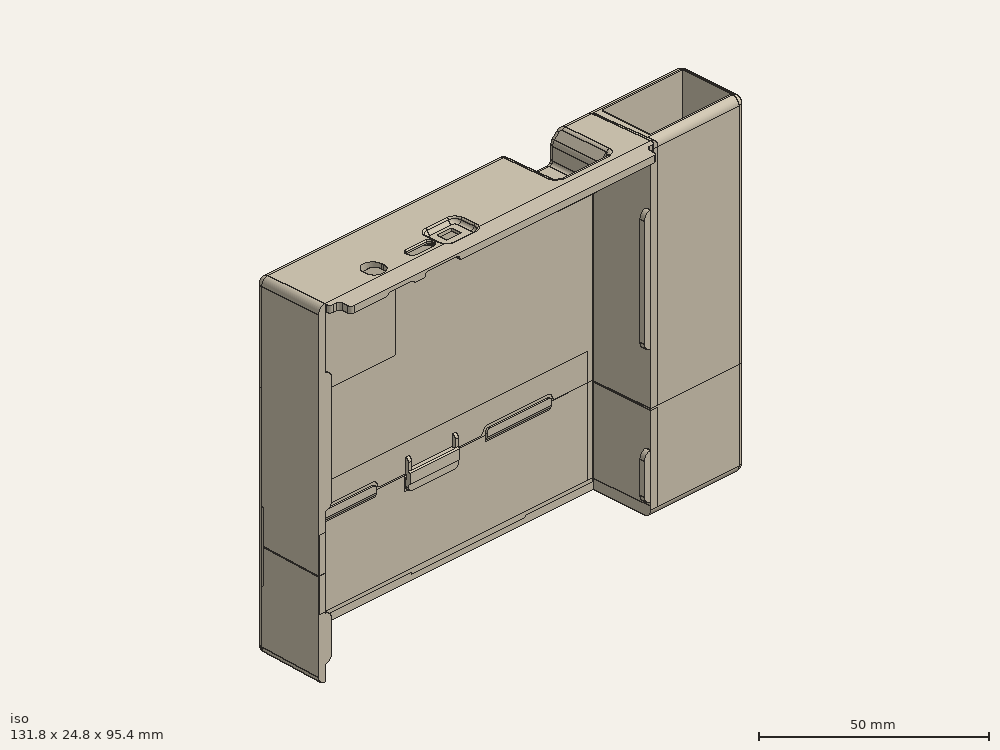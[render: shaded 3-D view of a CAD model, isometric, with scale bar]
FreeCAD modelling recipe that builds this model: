
FCSTD DOCUMENT  (FreeCAD 0.20R29177 +233 (Git))
Label: N2CaseOnePeice_10_12_2022
License: All rights reserved
LicenseURL: http://en.wikipedia.org/wiki/All_rights_reserved
objects: Part::Box×24, Part::Cylinder×12, Part::MultiFuse×11, Part::Cut×10, Part::Sphere×4, Part::Feature×2, Sketcher::SketchObject×2, PartDesign::Pad×2, PartDesign::Body×2
note: 71 computed .brp shape members not serialized (recipe doc carries the construction recipe); baked Part::Feature solids carry a one-line shape summary decoded from their .brp

FEATURE [Part::Feature] Solid  label="N2_BOTTOM_COVER"
  shape: bbox 104.6 x 25.21 x 71.78 mm, 343 faces (baked)
FEATURE [Part::Feature] Solid001  label="N2_TOP_COVER"
  shape: bbox 104.6 x 24.81 x 29.22 mm, 349 faces (baked)
FEATURE [Part::Box] Box  label="Cube"
  AttacherType = Attacher::AttachEngine3D
  Height = 15
  Length = 62.5
  Placement = pos=(-49,18,44) rot=(0,1,0;1.5708rad)
  Width = 2
FEATURE [Part::MultiFuse] Fusion  label="BottomCover"
  Shapes = -> [Solid,Box]
FEATURE [Part::Box] Box001  label="Cube001"
  AttacherType = Attacher::AttachEngine3D
  Height = 15
  Length = 97.5
  Placement = pos=(48.5,20,-3.5) rot=(0,1,0;3.14159rad)
  Width = 2
FEATURE [Part::Cut] Cut
  Base = -> Fusion
  Tool = -> Box001
FEATURE [Part::Box] Box002  label="usbEthernet"
  AttacherType = Attacher::AttachEngine3D
  Height = 25
  Length = 72
  Placement = pos=(52.5,2.6,47.4) rot=(0,1,0;1.5708rad)
  Width = 15
FEATURE [Part::Box] Box003  label="usbEthernetCover"
  AttacherType = Attacher::AttachEngine3D
  Height = 27.5
  Length = 72
  Placement = pos=(50.5,2.2,47.4) rot=(0,1,0;1.5708rad)
  Width = 15.85
FEATURE [Part::Box] Box004  label="usbEthernetCover001"
  AttacherType = Attacher::AttachEngine3D
  Height = 27.52
  Length = 65.19
  Placement = pos=(49.98,17.6,45.39) rot=(0,1,0;1.5708rad)
  Width = 2.4
FEATURE [Part::Box] Box005  label="usbEthernetCover002"
  AttacherType = Attacher::AttachEngine3D
  Height = 2
  Length = 65.19
  Placement = pos=(77.5,2.2,45.39) rot=(0,1,0;1.5708rad)
  Width = 15.8
FEATURE [Part::Cylinder] Cylinder
  Angle = 90
  AttacherType = Attacher::AttachEngine3D
  FirstAngle = 0
  Height = 65.2
  Placement = pos=(77.5,2.2,-19.8) rot=(0,0,-1;1.5708rad)
  Radius = 2
  SecondAngle = 0
FEATURE [Part::Cylinder] Cylinder001
  Angle = 90
  AttacherType = Attacher::AttachEngine3D
  FirstAngle = 0
  Height = 27.5
  Placement = pos=(77.5,18,45.4) rot=(0,-1,0;1.5708rad)
  Radius = 2
  SecondAngle = 0
FEATURE [Part::Cylinder] Cylinder002
  Angle = 90
  AttacherType = Attacher::AttachEngine3D
  FirstAngle = 0
  Height = 15.8
  Placement = pos=(77.5,2.2,45.4) rot=(0.57735,0.57735,0.57735;4.18879rad)
  Radius = 2
  SecondAngle = 0
FEATURE [Part::Cylinder] Cylinder003
  Angle = 90
  AttacherType = Attacher::AttachEngine3D
  FirstAngle = 0
  Height = 65.2
  Placement = pos=(77.5,18,-19.8) rot=(0,0,1;0rad)
  Radius = 2
  SecondAngle = 0
FEATURE [Part::Box] Box006  label="usbEthernetCover003"
  AttacherType = Attacher::AttachEngine3D
  Height = 27.2
  Length = 65.19
  Placement = pos=(50.3,0.2,45.39) rot=(0,1,0;1.5708rad)
  Width = 2.4
FEATURE [Part::Cylinder] Cylinder004
  Angle = 90
  AttacherType = Attacher::AttachEngine3D
  FirstAngle = 0
  Height = 26.4
  Placement = pos=(77.5,2.2,45.4) rot=(0.57735,-0.57735,-0.57735;2.0944rad)
  Radius = 2
  SecondAngle = 0
FEATURE [Part::Sphere] Sphere
  Angle1 = -90
  Angle2 = 90
  Angle3 = 360
  AttacherType = Attacher::AttachEngine3D
  Placement = pos=(77.5,18,45.4) rot=(0,0,1;0rad)
  Radius = 2
FEATURE [Part::Sphere] Sphere001
  Angle1 = -90
  Angle2 = 90
  Angle3 = 360
  AttacherType = Attacher::AttachEngine3D
  Placement = pos=(77.5,2.2,45.4) rot=(0,0,1;0rad)
  Radius = 2
FEATURE [Part::MultiFuse] Fusion001  label="usbCover"
  Shapes = -> [Box003,Box004,Box005,Cylinder,Cylinder001,Cylinder002,Cylinder003,Box006,Cylinder004,Sphere,Sphere001]
FEATURE [Part::MultiFuse] Fusion002
  Shapes = -> [Cut,Fusion001]
FEATURE [Part::Cut] Cut001  label="front"
  Base = -> Fusion002
  Tool = -> Box002
FEATURE [Part::Box] Box007  label="Cube002"
  AttacherType = Attacher::AttachEngine3D
  Height = 10
  Length = 30
  Placement = pos=(79.5,0,-19.8) rot=(0,1,0;3.14159rad)
  Width = 20
FEATURE [Part::Cut] Cut002
  Base = -> Cut001
  Tool = -> Box007
FEATURE [Part::Box] Box008  label="Cube003"
  AttacherType = Attacher::AttachEngine3D
  Height = 10
  Length = 30
  Placement = pos=(79.5,0,-19.8) rot=(0,1,0;3.14159rad)
  Width = 20
FEATURE [Part::Cut] Cut003  label="front001"
  Base = -> Cut002
  Tool = -> Box008
FEATURE [Part::Box] Box009  label="usbEthernet001"
  AttacherType = Attacher::AttachEngine3D
  Height = 25
  Length = 72
  Placement = pos=(52.5,2.6,6.3) rot=(0,1,0;1.5708rad)
  Width = 15
FEATURE [Part::Box] Box010  label="usbEthernetCover004"
  AttacherType = Attacher::AttachEngine3D
  Height = 27.5
  Length = 72
  Placement = pos=(50.5,2.2,-19.8) rot=(0,1,0;1.5708rad)
  Width = 15.85
FEATURE [Part::Box] Box011  label="usbEthernetCover005"
  AttacherType = Attacher::AttachEngine3D
  Height = 27.52
  Length = 65.19
  Placement = pos=(49.98,17.6,-19.8) rot=(0,1,0;1.5708rad)
  Width = 2.4
FEATURE [Part::Box] Box012  label="usbEthernetCover006"
  AttacherType = Attacher::AttachEngine3D
  Height = 2
  Length = 65.19
  Placement = pos=(77.5,2.2,-19.8) rot=(0,1,0;1.5708rad)
  Width = 15.8
FEATURE [Part::Box] Box013  label="usbEthernetCover007"
  AttacherType = Attacher::AttachEngine3D
  Height = 27.2
  Length = 65.19
  Placement = pos=(50.3,0.2,-19.8) rot=(0,1,0;1.5708rad)
  Width = 2.4
FEATURE [Part::Box] Box016  label="Cube005"
  AttacherType = Attacher::AttachEngine3D
  Height = 50
  Length = 29.5
  Placement = pos=(79.5,0,-45.4) rot=(0,1,0;3.14159rad)
  Width = 20
FEATURE [Part::MultiFuse] Fusion003
  Shapes = -> [Solid001,Box010,Box011,Box012,Box013]
FEATURE [Part::Cut] Cut004
  Base = -> Fusion003
  Tool = -> Box016
FEATURE [Part::Cut] Cut005
  Base = -> Cut004
  Tool = -> Box009
FEATURE [Part::Box] Box017  label="Cube006"
  AttacherType = Attacher::AttachEngine3D
  Height = 50
  Length = 23.5
  Placement = pos=(73.4,17.6,-45.39) rot=(0,1,0;3.14159rad)
  Width = 20
FEATURE [Part::Cut] Cut006
  Base = -> Cut005
  Tool = -> Box017
FEATURE [Part::Cylinder] Cylinder005
  Angle = 90
  AttacherType = Attacher::AttachEngine3D
  FirstAngle = 0
  Height = 65.2
  Placement = pos=(77.5,2.2,-45.4) rot=(0,0,-1;1.5708rad)
  Radius = 2
  SecondAngle = 0
FEATURE [Part::Cylinder] Cylinder006
  Angle = 90
  AttacherType = Attacher::AttachEngine3D
  FirstAngle = 0
  Height = 27.5
  Placement = pos=(77.5,18,-45.4) rot=(0,-1,0;1.5708rad)
  Radius = 2
  SecondAngle = 0
FEATURE [Part::Cylinder] Cylinder007
  Angle = 90
  AttacherType = Attacher::AttachEngine3D
  FirstAngle = 0
  Height = 15.8
  Placement = pos=(77.5,2.2,-45.4) rot=(-1,0,0;1.5708rad)
  Radius = 2
  SecondAngle = 0
FEATURE [Part::Cylinder] Cylinder008
  Angle = 90
  AttacherType = Attacher::AttachEngine3D
  FirstAngle = 0
  Height = 65.2
  Placement = pos=(77.5,18,-45.4) rot=(0,0,1;0rad)
  Radius = 2
  SecondAngle = 0
FEATURE [Part::Cylinder] Cylinder009
  Angle = 90
  AttacherType = Attacher::AttachEngine3D
  FirstAngle = 0
  Height = 27.6
  Placement = pos=(77.5,2.2,-45.4) rot=(0.707107,0,-0.707107;3.14159rad)
  Radius = 2
  SecondAngle = 0
FEATURE [Part::Cylinder] Cylinder010
  Angle = 90
  AttacherType = Attacher::AttachEngine3D
  FirstAngle = 0
  Height = 27.6
  Placement = pos=(77.5,18,-45.4) rot=(0.57735,0.57735,-0.57735;4.18879rad)
  Radius = 2
  SecondAngle = 0
FEATURE [Part::Box] Box018  label="Cube007"
  AttacherType = Attacher::AttachEngine3D
  Height = 2
  Length = 27.6
  Placement = pos=(49.9,18,-45.4) rot=(1,0,0;3.14159rad)
  Width = 15.8
FEATURE [Part::Box] Box019  label="usbEthernet002"
  AttacherType = Attacher::AttachEngine3D
  Height = 25
  Length = 72
  Placement = pos=(52.5,2.6,-2.5) rot=(0,1,0;1.5708rad)
  Width = 15
FEATURE [Part::Sphere] Sphere002
  Angle1 = -90
  Angle2 = 90
  Angle3 = 360
  AttacherType = Attacher::AttachEngine3D
  Placement = pos=(77.5,18,-45.4) rot=(0,0,1;0rad)
  Radius = 2
FEATURE [Part::Sphere] Sphere003
  Angle1 = -90
  Angle2 = 90
  Angle3 = 360
  AttacherType = Attacher::AttachEngine3D
  Placement = pos=(77.5,2.2,-45.4) rot=(0,0,1;0rad)
  Radius = 2
FEATURE [Part::Box] Box020  label="Cube008"
  AttacherType = Attacher::AttachEngine3D
  Height = 40
  Length = 10
  Placement = pos=(73.6,0,-19.8) rot=(0,0,1;0rad)
  Width = 22
FEATURE [Part::MultiFuse] Fusion004  label="cuts"
  Shapes = -> [Box020,Box019]
FEATURE [Part::MultiFuse] Fusion005
  Shapes = -> [Sphere003,Cut006,Cylinder005,Cylinder006,Cylinder007,Cylinder008,Cylinder009,Cylinder010,Box018,Sphere002]
FEATURE [Part::Cut] Cut007  label="back"
  Base = -> Fusion005
  Tool = -> Fusion004
FEATURE [Part::Box] Box021  label="Cube009"
  AttacherType = Attacher::AttachEngine3D
  Height = 32.5
  Length = 97.5
  Placement = pos=(48.5,18,-11.9) rot=(0,1,0;3.14159rad)
  Width = 2
FEATURE [Part::Box] Box068  label="logoBase001"
  AttacherType = Attacher::AttachEngine3D
  Height = 30
  Length = 35
  Placement = pos=(21.5,-44,15.25) rot=(0,0,1;0rad)
  Width = 1.8
FEATURE [Sketcher::SketchObject] Sketch001
  FullyConstrained = false
  MapMode = 5
  Support = -> [XY_Plane001]
  sketch-geometry (205):
    g0: LineSegment StartX=-15.0667 StartY=-2.9879 StartZ=0 EndX=-14.4175 EndY=-3.20194 EndZ=0
    g1: LineSegment StartX=-14.1386 StartY=-3.3581 StartZ=0 EndX=-13.8673 EndY=-3.55064 EndZ=0
    g2: LineSegment StartX=-10.8098 StartY=-4.00788 StartZ=0 EndX=-10.5716 EndY=-4.29909 EndZ=0
    g3: LineSegment StartX=-10.5716 StartY=-4.29909 StartZ=0 EndX=-10.1338 EndY=-4.33136 EndZ=0
    g4: LineSegment StartX=-10.1338 StartY=-4.33136 StartZ=0 EndX=-9.89036 EndY=-4.3898 EndZ=0
    g5: LineSegment StartX=-9.51656 StartY=-5.73022 StartZ=0 EndX=-9.24931 EndY=-5.76229 EndZ=0
    g6: LineSegment StartX=-9.24931 StartY=-5.76229 StartZ=0 EndX=-8.92861 EndY=-5.90126 EndZ=0
    g7: LineSegment StartX=-8.92861 StartY=-5.90126 StartZ=0 EndX=-8.54378 EndY=-5.86384 EndZ=0
    g8: LineSegment StartX=-8.54378 StartY=-5.86384 StartZ=0 EndX=-7.71788 EndY=-5.75845 EndZ=0
    g9: LineSegment StartX=-7.71788 StartY=-5.75845 StartZ=0 EndX=-7.37291 EndY=-5.97257 EndZ=0
    g10: LineSegment StartX=-7.37291 StartY=-5.97257 StartZ=0 EndX=-6.72487 EndY=-5.72038 EndZ=0
    g11: LineSegment StartX=-6.72487 StartY=-5.72038 StartZ=0 EndX=-6.27066 EndY=-5.69481 EndZ=0
    g12: LineSegment StartX=-6.27066 StartY=-5.69481 StartZ=0 EndX=-6.06223 EndY=-5.80493 EndZ=0
    g13: LineSegment StartX=-6.06223 StartY=-5.80493 StartZ=0 EndX=-5.35089 EndY=-5.48914 EndZ=0
    g14: LineSegment StartX=-5.35089 StartY=-5.48914 StartZ=0 EndX=-5.02402 EndY=-5.48914 EndZ=0
    g15: LineSegment StartX=-5.02402 StartY=-5.48914 StartZ=0 EndX=-4.80126 EndY=-5.53132 EndZ=0
    g16: LineSegment StartX=-4.80126 StartY=-5.53132 StartZ=0 EndX=-4.19735 EndY=-5.16248 EndZ=0
    g17: LineSegment StartX=-3.75191 StartY=-4.97251 StartZ=0 EndX=-3.37714 EndY=-4.97251 EndZ=0
    g18: LineSegment StartX=-3.37714 StartY=-4.97251 StartZ=0 EndX=-2.81898 EndY=-4.45422 EndZ=0
    g19: LineSegment StartX=-2.81898 StartY=-4.45422 StartZ=0 EndX=-2.62761 EndY=-4.34259 EndZ=0
    g20: LineSegment StartX=-2.62761 StartY=-4.34259 StartZ=0 EndX=-2.15112 EndY=-4.35765 EndZ=0
    g21: LineSegment StartX=-2.38042 StartY=-4.51801 StartZ=0 EndX=-3.18577 EndY=-5.42702 EndZ=0
    g22: LineSegment StartX=-3.18577 StartY=-5.42702 StartZ=0 EndX=-3.61318 EndY=-6.05824 EndZ=0
    g23: LineSegment StartX=-3.61318 StartY=-6.05824 StartZ=0 EndX=-3.7111 EndY=-6.64579 EndZ=0
    g24: LineSegment StartX=-3.7111 StartY=-6.64579 StartZ=0 EndX=-3.83514 EndY=-7.15501 EndZ=0
    g25: LineSegment StartX=-3.83514 StartY=-7.15501 StartZ=0 EndX=-3.75878 EndY=-7.50876 EndZ=0
    g26: LineSegment StartX=-3.75878 StartY=-7.50876 StartZ=0 EndX=-3.70596 EndY=-7.68135 EndZ=0
    g27: LineSegment StartX=-3.70596 StartY=-7.68135 StartZ=0 EndX=-3.53967 EndY=-7.85202 EndZ=0
    g28: LineSegment StartX=-3.53967 StartY=-7.85202 StartZ=0 EndX=-3.4685 EndY=-8.65617 EndZ=0
    g29: LineSegment StartX=-3.27268 StartY=-8.56671 StartZ=0 EndX=-3.16823 EndY=-8.76909 EndZ=0
    g30: LineSegment StartX=-3.07088 StartY=-9.32083 StartZ=0 EndX=-2.84207 EndY=-9.3355 EndZ=0
    g31: LineSegment StartX=-2.84207 StartY=-9.3355 StartZ=0 EndX=-2.45193 EndY=-10.0982 EndZ=0
    g32: LineSegment StartX=-2.45193 StartY=-10.0982 StartZ=0 EndX=-2.24953 EndY=-10.1304 EndZ=0
    g33: LineSegment StartX=-2.24953 StartY=-10.1304 StartZ=0 EndX=-0.96042 EndY=-11.8753 EndZ=0
    g34: LineSegment StartX=-0.96042 StartY=-11.8753 StartZ=0 EndX=-0.153326 EndY=-11.3889 EndZ=0
    g35: LineSegment StartX=-0.153326 StartY=-11.3889 StartZ=0 EndX=0.461347 EndY=-10.7689 EndZ=0
    g36: LineSegment StartX=0.461347 StartY=-10.7689 StartZ=0 EndX=0.669802 EndY=-10.7261 EndZ=0
    g37: LineSegment StartX=0.669802 StartY=-10.7261 StartZ=0 EndX=1.31724 EndY=-9.70998 EndZ=0
    g38: LineSegment StartX=1.31724 StartY=-9.70998 StartZ=0 EndX=1.51826 EndY=-9.65081 EndZ=0
    g39: LineSegment StartX=1.51826 StartY=-9.65081 StartZ=0 EndX=1.74022 EndY=-9.08937 EndZ=0
    g40: LineSegment StartX=1.74022 StartY=-9.08937 StartZ=0 EndX=2.02094 EndY=-9.04367 EndZ=0
    g41: LineSegment StartX=2.02094 StartY=-9.04367 StartZ=0 EndX=2.39306 EndY=-7.80327 EndZ=0
    g42: LineSegment StartX=2.39306 StartY=-7.80327 StartZ=0 EndX=2.58839 EndY=-7.69871 EndZ=0
    g43: LineSegment StartX=2.6542 StartY=-7.03945 StartZ=0 EndX=2.86963 EndY=-6.81749 EndZ=0
    g44: LineSegment StartX=2.86963 StartY=-6.81749 StartZ=0 EndX=3.0916 EndY=-6.92847 EndZ=0
    g45: LineSegment StartX=3.0916 StartY=-6.92847 StartZ=0 EndX=3.79666 EndY=-7.57478 EndZ=0
    g46: LineSegment StartX=3.79666 StartY=-7.57478 StartZ=0 EndX=3.93376 EndY=-7.50297 EndZ=0
    g47: LineSegment StartX=3.93376 StartY=-7.50297 StartZ=0 EndX=4.46256 EndY=-7.97301 EndZ=0
    g48: LineSegment StartX=4.46256 StartY=-7.97301 StartZ=0 EndX=4.68452 EndY=-7.92079 EndZ=0
    g49: LineSegment StartX=4.68452 StartY=-7.92079 StartZ=0 EndX=5.1154 EndY=-8.34513 EndZ=0
    g50: LineSegment StartX=5.1154 StartY=-8.34513 StartZ=0 EndX=5.32431 EndY=-8.28637 EndZ=0
    g51: LineSegment StartX=5.32431 StartY=-8.28637 StartZ=0 EndX=6.23668 EndY=-8.79564 EndZ=0
    g52: LineSegment StartX=6.23668 StartY=-8.79564 StartZ=0 EndX=6.50362 EndY=-8.76631 EndZ=0
    g53: LineSegment StartX=6.50362 StartY=-8.76631 StartZ=0 EndX=7.14802 EndY=-9.05537 EndZ=0
    g54: LineSegment StartX=7.14802 StartY=-9.05537 StartZ=0 EndX=8.04883 EndY=-9.18613 EndZ=0
    g55: LineSegment StartX=8.04883 StartY=-9.18613 StartZ=0 EndX=8.36847 EndY=-7.93662 EndZ=0
    g56: LineSegment StartX=8.36847 StartY=-7.93662 StartZ=0 EndX=8.49923 EndY=-7.79133 EndZ=0
    g57: LineSegment StartX=8.49923 StartY=-7.79133 StartZ=0 EndX=8.43477 EndY=-6.72206 EndZ=0
    g58: LineSegment StartX=8.43477 StartY=-6.72206 StartZ=0 EndX=8.58621 EndY=-6.47988 EndZ=0
    g59: LineSegment StartX=8.58621 StartY=-6.47988 StartZ=0 EndX=8.32296 EndY=-5.53178 EndZ=0
    g60: LineSegment StartX=8.32296 StartY=-5.53178 StartZ=0 EndX=8.43984 EndY=-5.19091 EndZ=0
    g61: LineSegment StartX=8.43984 StartY=-5.19091 StartZ=0 EndX=8.07426 EndY=-4.39307 EndZ=0
    g62: LineSegment StartX=8.07426 StartY=-4.39307 StartZ=0 EndX=8.04236 EndY=-4.17777 EndZ=0
    g63: LineSegment StartX=8.04236 StartY=-4.17777 StartZ=0 EndX=8.0902 EndY=-3.99438 EndZ=0
    g64: LineSegment StartX=8.4103 StartY=-4.11103 StartZ=0 EndX=8.72013 EndY=-4.0502 EndZ=0
    g65: LineSegment StartX=8.72013 StartY=-4.0502 StartZ=0 EndX=9.31817 EndY=-4.0502 EndZ=0
    g66: LineSegment StartX=9.31817 StartY=-4.0502 StartZ=0 EndX=9.82964 EndY=-4.15887 EndZ=0
    g67: LineSegment StartX=10.1326 StartY=-3.9675 StartZ=0 EndX=10.5175 EndY=-3.9623 EndZ=0
    g68: LineSegment StartX=10.5175 StartY=-3.9623 StartZ=0 EndX=10.8831 EndY=-3.97536 EndZ=0
    g69: LineSegment StartX=10.8831 StartY=-3.97536 StartZ=0 EndX=11.2245 EndY=-4.09431 EndZ=0
    g70: LineSegment StartX=11.2245 StartY=-4.09431 StartZ=0 EndX=11.6861 EndY=-3.91007 EndZ=0
    g71: LineSegment StartX=11.6861 StartY=-3.91007 StartZ=0 EndX=12.1039 EndY=-3.88396 EndZ=0
    g72: LineSegment StartX=12.1039 StartY=-3.88396 StartZ=0 EndX=12.6 EndY=-3.9623 EndZ=0
    g73: LineSegment StartX=12.6 StartY=-3.9623 StartZ=0 EndX=13.5793 EndY=-3.87743 EndZ=0
    g74: LineSegment StartX=13.5793 StartY=-3.87743 StartZ=0 EndX=14.3888 EndY=-3.74687 EndZ=0
    g75: LineSegment StartX=14.3888 StartY=-3.74687 StartZ=0 EndX=14.7544 EndY=-3.68158 EndZ=0
    g76: LineSegment StartX=14.7544 StartY=-3.68158 StartZ=0 EndX=15.2767 EndY=-3.75339 EndZ=0
    g77: LineSegment StartX=15.2767 StartY=-3.75339 StartZ=0 EndX=15.0432 EndY=-3.24137 EndZ=0
    g78: LineSegment StartX=15.0432 StartY=-3.24137 StartZ=0 EndX=14.5209 EndY=-2.51672 EndZ=0
    g79: LineSegment StartX=14.5209 StartY=-2.51672 StartZ=0 EndX=14.0378 EndY=-1.99445 EndZ=0
    g80: LineSegment StartX=14.0378 StartY=-1.99445 StartZ=0 EndX=13.2802 EndY=-1.54625 EndZ=0
    g81: LineSegment StartX=13.2802 StartY=-1.54625 StartZ=0 EndX=13.0438 EndY=-1.23117 EndZ=0
    g82: LineSegment StartX=13.0438 StartY=-1.23117 StartZ=0 EndX=12.1074 EndY=-0.797939 EndZ=0
    g83: LineSegment StartX=12.1074 StartY=-0.797939 StartZ=0 EndX=11.3804 EndY=-0.250878 EndZ=0
    g84: LineSegment StartX=11.3804 StartY=-0.250878 StartZ=0 EndX=10.4396 EndY=0.304889 EndZ=0
    g85: LineSegment StartX=10.4396 StartY=0.304889 StartZ=0 EndX=9.59526 EndY=0.727998 EndZ=0
    g86: LineSegment StartX=9.59526 StartY=0.727998 StartZ=0 EndX=8.53624 EndY=0.97306 EndZ=0
    g87: LineSegment StartX=8.53624 StartY=0.97306 StartZ=0 EndX=7.199 EndY=0.97306 EndZ=0
    g88: LineSegment StartX=7.199 StartY=0.97306 StartZ=0 EndX=5.77932 EndY=0.795578 EndZ=0
    g89: LineSegment StartX=5.77932 StartY=0.795578 StartZ=0 EndX=5.60186 EndY=0.795578 EndZ=0
    g90: LineSegment StartX=5.60186 StartY=0.795578 StartZ=0 EndX=5.83178 EndY=0.981815 EndZ=0
    g91: LineSegment StartX=5.83178 StartY=0.981815 StartZ=0 EndX=6.25403 EndY=1.1582 EndZ=0
    g92: LineSegment StartX=6.30214 StartY=1.38269 StartZ=0 EndX=7.17987 EndY=1.70686 EndZ=0
    g93: LineSegment StartX=7.17987 StartY=1.70686 StartZ=0 EndX=7.44682 EndY=1.79438 EndZ=0
    g94: LineSegment StartX=7.44682 StartY=1.79438 StartZ=0 EndX=7.49058 EndY=2.12696 EndZ=0
    g95: LineSegment StartX=7.49058 StartY=2.12696 StartZ=0 EndX=8.30058 EndY=2.66839 EndZ=0
    g96: LineSegment StartX=8.30058 StartY=2.66839 StartZ=0 EndX=8.68575 EndY=2.81854 EndZ=0
    g97: LineSegment StartX=8.68575 StartY=2.81854 StartZ=0 EndX=8.68575 EndY=3.12537 EndZ=0
    g98: LineSegment StartX=8.68575 StartY=3.12537 StartZ=0 EndX=8.89508 EndY=3.18684 EndZ=0
    g99: LineSegment StartX=8.89508 StartY=3.18684 StartZ=0 EndX=9.63492 EndY=4.06602 EndZ=0
    g100: LineSegment StartX=9.63492 StartY=4.06602 StartZ=0 EndX=9.62638 EndY=4.32743 EndZ=0
    g101: LineSegment StartX=9.62638 StartY=4.32743 StartZ=0 EndX=10.2068 EndY=5.18314 EndZ=0
    g102: LineSegment StartX=10.2068 StartY=5.18314 StartZ=0 EndX=9.25518 EndY=5.64445 EndZ=0
    g103: LineSegment StartX=9.1102 StartY=5.87597 StartZ=0 EndX=8.32132 EndY=5.97336 EndZ=0
    g104: LineSegment StartX=8.32132 StartY=5.97336 StartZ=0 EndX=8.15466 EndY=6.06625 EndZ=0
    g105: LineSegment StartX=7.63471 StartY=6.13088 StartZ=0 EndX=7.56391 EndY=6.33267 EndZ=0
    g106: LineSegment StartX=7.56391 StartY=6.33267 StartZ=0 EndX=6.74832 EndY=6.35496 EndZ=0
    g107: LineSegment StartX=6.74832 StartY=6.35496 StartZ=0 EndX=6.46819 EndY=6.29526 EndZ=0
    g108: LineSegment StartX=6.46819 StartY=6.29526 StartZ=0 EndX=6.27042 EndY=6.61061 EndZ=0
    g109: LineSegment StartX=6.27042 StartY=6.61061 StartZ=0 EndX=5.40453 EndY=6.33267 EndZ=0
    g110: LineSegment StartX=5.40453 StartY=6.33267 StartZ=0 EndX=5.27091 EndY=6.47164 EndZ=0
    g111: LineSegment StartX=5.27091 StartY=6.47164 StartZ=0 EndX=4.56942 EndY=6.24725 EndZ=0
    g112: LineSegment StartX=4.56942 StartY=6.24725 StartZ=0 EndX=4.44161 EndY=6.40652 EndZ=0
    g113: LineSegment StartX=4.44161 StartY=6.40652 StartZ=0 EndX=3.4195 EndY=5.94588 EndZ=0
    g114: LineSegment StartX=3.4195 StartY=5.94588 StartZ=0 EndX=3.29192 EndY=6.1532 EndZ=0
    g115: LineSegment StartX=3.29192 StartY=6.1532 StartZ=0 EndX=2.15964 EndY=5.49137 EndZ=0
    g116: LineSegment StartX=2.15964 StartY=5.49137 StartZ=0 EndX=2.00016 EndY=5.69869 EndZ=0
    g117: LineSegment StartX=2.00016 StartY=5.69869 StartZ=0 EndX=1.6185 EndY=5.34828 EndZ=0
    g118: LineSegment StartX=1.6185 StartY=5.34828 StartZ=0 EndX=1.45984 EndY=5.94974 EndZ=0
    g119: LineSegment StartX=1.38165 StartY=6.28651 StartZ=0 EndX=1.14534 EndY=6.29963 EndZ=0
    g120: LineSegment StartX=0.348522 StartY=7.29544 StartZ=0 EndX=0.126706 EndY=7.68126 EndZ=0
    g121: LineSegment StartX=0.126706 StartY=7.68126 StartZ=0 EndX=-0.415308 EndY=8.18163 EndZ=0
    g122: LineSegment StartX=-0.415308 StartY=8.18163 StartZ=0 EndX=-0.872658 EndY=8.6237 EndZ=0
    g123: LineSegment StartX=-0.872658 StartY=8.6237 StartZ=0 EndX=-1.12074 EndY=8.64329 EndZ=0
    g124: LineSegment StartX=-1.12074 StartY=8.64329 StartZ=0 EndX=-1.79316 EndY=9.11986 EndZ=0
    g125: LineSegment StartX=-1.79316 StartY=9.11986 StartZ=0 EndX=-2.31488 EndY=9.12122 EndZ=0
    g126: LineSegment StartX=-2.31488 StartY=9.12122 StartZ=0 EndX=-2.71321 EndY=9.13846 EndZ=0
    g127: LineSegment StartX=-2.71321 StartY=9.13846 StartZ=0 EndX=-2.88425 EndY=9.34157 EndZ=0
    g128: LineSegment StartX=-2.88425 StartY=9.34157 StartZ=0 EndX=-3.16779 EndY=9.26454 EndZ=0
    g129: LineSegment StartX=-3.70739 StartY=9.82796 StartZ=0 EndX=-4.04915 EndY=9.7003 EndZ=0
    g130: LineSegment StartX=-4.04915 StartY=9.7003 StartZ=0 EndX=-4.42988 EndY=10.011 EndZ=0
    g131: LineSegment StartX=-5.98947 StartY=10.3656 StartZ=0 EndX=-7.32605 EndY=10.4108 EndZ=0
    g132: LineSegment StartX=-7.25254 StartY=9.13254 StartZ=0 EndX=-7.36878 EndY=8.7693 EndZ=0
    g133: LineSegment StartX=-7.36878 StartY=8.7693 StartZ=0 EndX=-7.2614 EndY=7.83762 EndZ=0
    g134: LineSegment StartX=-7.2614 StartY=7.83762 StartZ=0 EndX=-7.41112 EndY=7.6042 EndZ=0
    g135: LineSegment StartX=-7.41112 StartY=7.6042 StartZ=0 EndX=-7.09216 EndY=6.74302 EndZ=0
    g136: LineSegment StartX=-7.09216 StartY=6.74302 StartZ=0 EndX=-7.10014 EndY=6.55962 EndZ=0
    g137: LineSegment StartX=-7.10014 StartY=6.55962 StartZ=0 EndX=-7.29151 EndY=6.3842 EndZ=0
    g138: LineSegment StartX=-7.29151 StartY=6.3842 StartZ=0 EndX=-6.74132 EndY=5.29976 EndZ=0
    g139: LineSegment StartX=-6.74132 StartY=5.29976 StartZ=0 EndX=-6.87495 EndY=5.02732 EndZ=0
    g140: LineSegment StartX=-6.87495 StartY=5.02732 StartZ=0 EndX=-6.31586 EndY=4.42065 EndZ=0
    g141: LineSegment StartX=-6.31586 StartY=4.42065 StartZ=0 EndX=-6.30396 EndY=4.19463 EndZ=0
    g142: LineSegment StartX=-6.30396 StartY=4.19463 StartZ=0 EndX=-6.05415 EndY=4.0043 EndZ=0
    g143: LineSegment StartX=-6.05415 StartY=4.0043 StartZ=0 EndX=-6.18501 EndY=3.95672 EndZ=0
    g144: LineSegment StartX=-6.18501 StartY=3.95672 StartZ=0 EndX=-5.54265 EndY=3.07645 EndZ=0
    g145: LineSegment StartX=-5.54265 StartY=3.07645 StartZ=0 EndX=-5.57833 EndY=2.90991 EndZ=0
    g146: LineSegment StartX=-5.57833 StartY=2.90991 StartZ=0 EndX=-5.1263 EndY=2.41029 EndZ=0
    g147: LineSegment StartX=-5.1263 StartY=2.41029 StartZ=0 EndX=-5.18578 EndY=2.26755 EndZ=0
    g148: LineSegment StartX=-5.18578 StartY=2.26755 StartZ=0 EndX=-4.73375 EndY=1.89878 EndZ=0
    g149: LineSegment StartX=-4.73375 StartY=1.89878 StartZ=0 EndX=-4.42446 EndY=1.5895 EndZ=0
    g150: LineSegment StartX=-4.42446 StartY=1.5895 StartZ=0 EndX=-5.31663 EndY=1.29211 EndZ=0
    g151: LineSegment StartX=-5.31663 StartY=1.29211 StartZ=0 EndX=-5.84004 EndY=1.08988 EndZ=0
    g152: LineSegment StartX=-5.84004 StartY=1.08988 StartZ=0 EndX=-6.04226 EndY=0.792495 EndZ=0
    g153: LineSegment StartX=-6.04226 StartY=0.792495 StartZ=0 EndX=-6.94632 EndY=0.994719 EndZ=0
    g154: LineSegment StartX=-6.94632 StartY=0.994719 StartZ=0 EndX=-7.19613 EndY=0.887659 EndZ=0
    g155: LineSegment StartX=-7.19613 StartY=0.887659 StartZ=0 EndX=-7.8147 EndY=1.0423 EndZ=0
    g156: LineSegment StartX=-7.8147 StartY=1.0423 StartZ=0 EndX=-8.02502 EndY=0.969153 EndZ=0
    g157: LineSegment StartX=-8.02502 StartY=0.969153 StartZ=0 EndX=-8.60267 EndY=1.03042 EndZ=0
    g158: LineSegment StartX=-8.60267 StartY=1.03042 StartZ=0 EndX=-8.8346 EndY=0.872878 EndZ=0
    g159: LineSegment StartX=-8.8346 StartY=0.872878 StartZ=0 EndX=-9.33349 EndY=0.929767 EndZ=0
    g160: LineSegment StartX=-9.33349 StartY=0.929767 StartZ=0 EndX=-9.66169 EndY=0.649695 EndZ=0
    g161: LineSegment StartX=-9.66169 StartY=0.649695 StartZ=0 EndX=-10.3249 EndY=0.649695 EndZ=0
    g162: LineSegment StartX=-10.3249 StartY=0.649695 StartZ=0 EndX=-11.0107 EndY=0.32425 EndZ=0
    g163: LineSegment StartX=-11.0107 StartY=0.32425 StartZ=0 EndX=-11.7283 EndY=0.053139 EndZ=0
    g164: LineSegment StartX=-11.7283 StartY=0.053139 StartZ=0 EndX=-12.2971 EndY=-0.13161 EndZ=0
    g165: LineSegment StartX=-12.2971 StartY=-0.13161 StartZ=0 EndX=-12.4212 EndY=-0.347049 EndZ=0
    g166: LineSegment StartX=-12.4212 StartY=-0.347049 StartZ=0 EndX=-13.296 EndY=-0.817096 EndZ=0
    g167: LineSegment StartX=-13.296 StartY=-0.817096 StartZ=0 EndX=-13.9227 EndY=-1.24144 EndZ=0
    g168: LineSegment StartX=-13.9227 StartY=-1.24144 StartZ=0 EndX=-14.1708 EndY=-1.59398 EndZ=0
    g169: LineSegment StartX=-14.1708 StartY=-1.59398 StartZ=0 EndX=-14.5386 EndY=-2.09216 EndZ=0
    g170: LineSegment StartX=-14.5386 StartY=-2.09216 StartZ=0 EndX=-14.7831 EndY=-2.4577 EndZ=0
    g171: LineSegment StartX=-14.7831 StartY=-2.4577 StartZ=0 EndX=-15.0667 EndY=-2.9879 EndZ=0
    g172: LineSegment StartX=7.82861 StartY=6.04487 StartZ=0 EndX=7.63471 EndY=6.13088 EndZ=0
    g173: LineSegment StartX=-14.4175 StartY=-3.20194 StartZ=0 EndX=-14.1386 EndY=-3.3581 EndZ=0
    g174: LineSegment StartX=-13.8673 StartY=-3.55064 StartZ=0 EndX=-13.4107 EndY=-3.57136 EndZ=0
    g175: LineSegment StartX=-13.1321 StartY=-3.61699 StartZ=0 EndX=-12.817 EndY=-3.62343 EndZ=0
    g176: LineSegment StartX=-12.817 StartY=-3.62343 StartZ=0 EndX=-12.4662 EndY=-3.85302 EndZ=0
    g177: LineSegment StartX=-13.4107 StartY=-3.57136 StartZ=0 EndX=-13.1321 EndY=-3.61699 EndZ=0
    g178: LineSegment StartX=-12.4662 StartY=-3.85302 StartZ=0 EndX=-11.8704 EndY=-3.85302 EndZ=0
    g179: LineSegment StartX=-11.8704 StartY=-3.85302 StartZ=0 EndX=-11.5204 EndY=-4.00836 EndZ=0
    g180: LineSegment StartX=-11.5204 StartY=-4.00836 StartZ=0 EndX=-11.1389 EndY=-4.05555 EndZ=0
    g181: LineSegment StartX=-11.1389 StartY=-4.05555 StartZ=0 EndX=-10.8098 EndY=-4.00788 EndZ=0
    g182: LineSegment StartX=-9.89036 StartY=-4.3898 StartZ=0 EndX=-9.99555 EndY=-4.87697 EndZ=0
    g183: LineSegment StartX=-9.99555 StartY=-4.87697 StartZ=0 EndX=-10.0894 EndY=-5.36391 EndZ=0
    g184: LineSegment StartX=-10.0894 StartY=-5.36391 StartZ=0 EndX=-10.107 EndY=-5.50471 EndZ=0
    g185: LineSegment StartX=-10.107 StartY=-5.50471 StartZ=0 EndX=-9.77848 EndY=-5.63965 EndZ=0
    g186: LineSegment StartX=-9.77848 StartY=-5.63965 StartZ=0 EndX=-9.51656 EndY=-5.73022 EndZ=0
    g187: LineSegment StartX=-4.19735 StartY=-5.16248 StartZ=0 EndX=-3.75191 EndY=-4.97251 EndZ=0
    g188: LineSegment StartX=-2.38042 StartY=-4.51801 StartZ=0 EndX=-2.15112 EndY=-4.35765 EndZ=0
    g189: LineSegment StartX=-3.4685 StartY=-8.65617 StartZ=0 EndX=-3.27268 EndY=-8.56671 EndZ=0
    g190: LineSegment StartX=-3.16823 StartY=-8.76909 StartZ=0 EndX=-3.07088 EndY=-9.32083 EndZ=0
    g191: LineSegment StartX=2.58839 StartY=-7.69871 StartZ=0 EndX=2.6542 EndY=-7.03945 EndZ=0
    g192: LineSegment StartX=8.0902 StartY=-3.99438 StartZ=0 EndX=8.4103 EndY=-4.11103 EndZ=0
    g193: LineSegment StartX=9.82964 StartY=-4.15887 StartZ=0 EndX=10.1326 EndY=-3.9675 EndZ=0
    g194: LineSegment StartX=6.30214 StartY=1.38269 StartZ=0 EndX=6.25403 EndY=1.1582 EndZ=0
    g195: LineSegment StartX=1.38165 StartY=6.28651 StartZ=0 EndX=1.45984 EndY=5.94974 EndZ=0
    g196: LineSegment StartX=0.348522 StartY=7.29544 StartZ=0 EndX=0.824344 EndY=6.91479 EndZ=0
    g197: LineSegment StartX=0.824344 StartY=6.91479 StartZ=0 EndX=1.14534 EndY=6.29963 EndZ=0
    g198: LineSegment StartX=-3.70739 StartY=9.82796 StartZ=0 EndX=-3.16779 EndY=9.26454 EndZ=0
    g199: LineSegment StartX=-5.98947 StartY=10.3656 StartZ=0 EndX=-5.43038 EndY=10.4489 EndZ=0
    g200: LineSegment StartX=-5.43038 StartY=10.4489 StartZ=0 EndX=-4.9791 EndY=10.1425 EndZ=0
    g201: LineSegment StartX=-4.42988 StartY=10.011 StartZ=0 EndX=-4.9791 EndY=10.1425 EndZ=0
    g202: LineSegment StartX=-7.25254 StartY=9.13254 StartZ=0 EndX=-7.32605 EndY=10.4108 EndZ=0
    g203: LineSegment StartX=7.82861 StartY=6.04487 StartZ=0 EndX=8.15466 EndY=6.06625 EndZ=0
    g204: LineSegment StartX=9.1102 StartY=5.87597 StartZ=0 EndX=9.25518 EndY=5.64445 EndZ=0
  constraints (114):
    c: Coincident(g4,g3)
    c: Coincident(g6,g5)
    c: Coincident(g8,g7)
    c: Coincident(g9,g8)
    c: Coincident(g10,g9)
    c: Coincident(g11,g10)
    c: Coincident(g13,g12)
    c: Coincident(g16,g15)
    c: Coincident(g22,g21)
    c: Coincident(g25,g24)
    c: Coincident(g26,g25)
    c: Coincident(g28,g27)
    c: Coincident(g33,g32)
    c: Coincident(g37,g36)
    c: Coincident(g38,g37)
    c: Coincident(g40,g39)
    c: Coincident(g44,g43)
    c: Coincident(g51,g50)
    c: Coincident(g52,g51)
    c: Coincident(g57,g56)
    c: Coincident(g58,g57)
    c: Coincident(g59,g58)
    c: Coincident(g61,g60)
    c: Coincident(g63,g62)
    c: Coincident(g66,g65)
    c: Coincident(g70,g69)
    c: Coincident(g72,g71)
    c: Coincident(g73,g72)
    c: Coincident(g74,g73)
    c: Coincident(g77,g76)
    c: Coincident(g80,g79)
    c: Coincident(g81,g80)
    c: Coincident(g83,g82)
    c: Coincident(g85,g84)
    c: Coincident(g86,g85)
    c: Coincident(g87,g86)
    c: Coincident(g89,g88)
    c: Coincident(g90,g89)
    c: Coincident(g91,g90)
    c: Coincident(g93,g92)
    c: Coincident(g95,g94)
    c: Coincident(g97,g96)
    c: Coincident(g98,g97)
    c: Coincident(g99,g98)
    c: Coincident(g100,g99)
    c: Coincident(g104,g103)
    c: Coincident(g106,g105)
    c: Coincident(g107,g106)
    c: Coincident(g111,g110)
    c: Coincident(g113,g112)
    c: Coincident(g118,g117)
    c: Coincident(g122,g121)
    c: Coincident(g126,g125)
    c: Coincident(g130,g129)
    c: Coincident(g133,g132)
    c: Coincident(g134,g133)
    c: Coincident(g135,g134)
    c: Coincident(g139,g138)
    c: Coincident(g142,g141)
    c: Coincident(g156,g155)
    c: Coincident(g157,g156)
    c: Coincident(g159,g158)
    c: Coincident(g161,g160)
    c: Coincident(g164,g163)
    c: Coincident(g165,g164)
    c: Coincident(g168,g167)
    c: Coincident(g169,g168)
    c: Coincident(g171,g170)
    c: Coincident(g171,g0)
    c: Coincident(g172,g105)
    c: DistanceX(g165) = -12.4212
    c: DistanceY(g165) = -0.347049
    c: Coincident(g173,g0)
    c: Coincident(g173,g1)
    c: Coincident(g174,g1)
    c: Coincident(g177,g174)
    c: Coincident(g177,g175)
    c: Coincident(g178,g176)
    c: Coincident(g181,g2)
    c: Coincident(g182,g4)
    c: Coincident(g186,g185)
    c: Coincident(g186,g5)
    c: Coincident(g187,g16)
    c: Coincident(g187,g17)
    c: Coincident(g188,g21)
    c: Coincident(g188,g20)
    c: Coincident(g189,g28)
    c: Coincident(g189,g29)
    c: Coincident(g190,g29)
    c: Coincident(g190,g30)
    c: Coincident(g191,g42)
    c: Coincident(g191,g43)
    c: Coincident(g192,g63)
    c: Coincident(g192,g64)
    c: Coincident(g193,g66)
    c: Coincident(g193,g67)
    c: Coincident(g194,g92)
    c: Coincident(g194,g91)
    c: Coincident(g195,g119)
    c: Coincident(g195,g118)
    c: Coincident(g196,g120)
    c: Coincident(g197,g119)
    c: Coincident(g198,g129)
    c: Coincident(g198,g128)
    c: Coincident(g199,g131)
    c: Coincident(g200,g199)
    c: Coincident(g201,g130)
    c: Coincident(g201,g200)
    c: Coincident(g202,g132)
    c: Coincident(g202,g131)
    c: Coincident(g203,g172)
    c: Coincident(g203,g104)
    c: Coincident(g204,g103)
    c: Coincident(g204,g102)
FEATURE [PartDesign::Pad] Pad001
  Direction = (0,0,1)
  Length = 3
  Length2 = 10
  Profile = -> Sketch001
  ReferenceAxis = -> Sketch001 [N_Axis]
  Type = 0
FEATURE [PartDesign::Body] Body001  label="logo002"
  Group = -> [Sketch001,Pad001]
  Origin = -> Origin001
  Placement = pos=(39.35,-43,30) rot=(1,0,0;1.5708rad)
  Tip = -> Pad001
FEATURE [Part::MultiFuse] Fusion040  label="logo003"
  Placement = pos=(-69,-26,58) rot=(1,0,0;3.14159rad)
  Shapes = -> [Body001,Box068]
FEATURE [Part::Cut] Cut008  label="front002"
  Base = -> Cut003
  Tool = -> Fusion040
FEATURE [Part::Box] Box069  label="logoBase002"
  AttacherType = Attacher::AttachEngine3D
  Height = 30
  Length = 35
  Placement = pos=(21.5,-44,15.25) rot=(0,0,1;0rad)
  Width = 1.8
FEATURE [Sketcher::SketchObject] Sketch002
  FullyConstrained = false
  MapMode = 5
  Support = -> [XY_Plane002]
  sketch-geometry (205):
    g0: LineSegment StartX=-15.0667 StartY=-2.9879 StartZ=0 EndX=-14.4175 EndY=-3.20194 EndZ=0
    g1: LineSegment StartX=-14.1386 StartY=-3.3581 StartZ=0 EndX=-13.8673 EndY=-3.55064 EndZ=0
    g2: LineSegment StartX=-10.8098 StartY=-4.00788 StartZ=0 EndX=-10.5716 EndY=-4.29909 EndZ=0
    g3: LineSegment StartX=-10.5716 StartY=-4.29909 StartZ=0 EndX=-10.1338 EndY=-4.33136 EndZ=0
    g4: LineSegment StartX=-10.1338 StartY=-4.33136 StartZ=0 EndX=-9.89036 EndY=-4.3898 EndZ=0
    g5: LineSegment StartX=-9.51656 StartY=-5.73022 StartZ=0 EndX=-9.24931 EndY=-5.76229 EndZ=0
    g6: LineSegment StartX=-9.24931 StartY=-5.76229 StartZ=0 EndX=-8.92861 EndY=-5.90126 EndZ=0
    g7: LineSegment StartX=-8.92861 StartY=-5.90126 StartZ=0 EndX=-8.54378 EndY=-5.86384 EndZ=0
    g8: LineSegment StartX=-8.54378 StartY=-5.86384 StartZ=0 EndX=-7.71788 EndY=-5.75845 EndZ=0
    g9: LineSegment StartX=-7.71788 StartY=-5.75845 StartZ=0 EndX=-7.37291 EndY=-5.97257 EndZ=0
    g10: LineSegment StartX=-7.37291 StartY=-5.97257 StartZ=0 EndX=-6.72487 EndY=-5.72038 EndZ=0
    g11: LineSegment StartX=-6.72487 StartY=-5.72038 StartZ=0 EndX=-6.27066 EndY=-5.69481 EndZ=0
    g12: LineSegment StartX=-6.27066 StartY=-5.69481 StartZ=0 EndX=-6.06223 EndY=-5.80493 EndZ=0
    g13: LineSegment StartX=-6.06223 StartY=-5.80493 StartZ=0 EndX=-5.35089 EndY=-5.48914 EndZ=0
    g14: LineSegment StartX=-5.35089 StartY=-5.48914 StartZ=0 EndX=-5.02402 EndY=-5.48914 EndZ=0
    g15: LineSegment StartX=-5.02402 StartY=-5.48914 StartZ=0 EndX=-4.80126 EndY=-5.53132 EndZ=0
    g16: LineSegment StartX=-4.80126 StartY=-5.53132 StartZ=0 EndX=-4.19735 EndY=-5.16248 EndZ=0
    g17: LineSegment StartX=-3.75191 StartY=-4.97251 StartZ=0 EndX=-3.37714 EndY=-4.97251 EndZ=0
    g18: LineSegment StartX=-3.37714 StartY=-4.97251 StartZ=0 EndX=-2.81898 EndY=-4.45422 EndZ=0
    g19: LineSegment StartX=-2.81898 StartY=-4.45422 StartZ=0 EndX=-2.62761 EndY=-4.34259 EndZ=0
    g20: LineSegment StartX=-2.62761 StartY=-4.34259 StartZ=0 EndX=-2.15112 EndY=-4.35765 EndZ=0
    g21: LineSegment StartX=-2.38042 StartY=-4.51801 StartZ=0 EndX=-3.18577 EndY=-5.42702 EndZ=0
    g22: LineSegment StartX=-3.18577 StartY=-5.42702 StartZ=0 EndX=-3.61318 EndY=-6.05824 EndZ=0
    g23: LineSegment StartX=-3.61318 StartY=-6.05824 StartZ=0 EndX=-3.7111 EndY=-6.64579 EndZ=0
    g24: LineSegment StartX=-3.7111 StartY=-6.64579 StartZ=0 EndX=-3.83514 EndY=-7.15501 EndZ=0
    g25: LineSegment StartX=-3.83514 StartY=-7.15501 StartZ=0 EndX=-3.75878 EndY=-7.50876 EndZ=0
    g26: LineSegment StartX=-3.75878 StartY=-7.50876 StartZ=0 EndX=-3.70596 EndY=-7.68135 EndZ=0
    g27: LineSegment StartX=-3.70596 StartY=-7.68135 StartZ=0 EndX=-3.53967 EndY=-7.85202 EndZ=0
    g28: LineSegment StartX=-3.53967 StartY=-7.85202 StartZ=0 EndX=-3.4685 EndY=-8.65617 EndZ=0
    g29: LineSegment StartX=-3.27268 StartY=-8.56671 StartZ=0 EndX=-3.16823 EndY=-8.76909 EndZ=0
    g30: LineSegment StartX=-3.07088 StartY=-9.32083 StartZ=0 EndX=-2.84207 EndY=-9.3355 EndZ=0
    g31: LineSegment StartX=-2.84207 StartY=-9.3355 StartZ=0 EndX=-2.45193 EndY=-10.0982 EndZ=0
    g32: LineSegment StartX=-2.45193 StartY=-10.0982 StartZ=0 EndX=-2.24953 EndY=-10.1304 EndZ=0
    g33: LineSegment StartX=-2.24953 StartY=-10.1304 StartZ=0 EndX=-0.96042 EndY=-11.8753 EndZ=0
    g34: LineSegment StartX=-0.96042 StartY=-11.8753 StartZ=0 EndX=-0.153326 EndY=-11.3889 EndZ=0
    g35: LineSegment StartX=-0.153326 StartY=-11.3889 StartZ=0 EndX=0.461347 EndY=-10.7689 EndZ=0
    g36: LineSegment StartX=0.461347 StartY=-10.7689 StartZ=0 EndX=0.669802 EndY=-10.7261 EndZ=0
    g37: LineSegment StartX=0.669802 StartY=-10.7261 StartZ=0 EndX=1.31724 EndY=-9.70998 EndZ=0
    g38: LineSegment StartX=1.31724 StartY=-9.70998 StartZ=0 EndX=1.51826 EndY=-9.65081 EndZ=0
    g39: LineSegment StartX=1.51826 StartY=-9.65081 StartZ=0 EndX=1.74022 EndY=-9.08937 EndZ=0
    g40: LineSegment StartX=1.74022 StartY=-9.08937 StartZ=0 EndX=2.02094 EndY=-9.04367 EndZ=0
    g41: LineSegment StartX=2.02094 StartY=-9.04367 StartZ=0 EndX=2.39306 EndY=-7.80327 EndZ=0
    g42: LineSegment StartX=2.39306 StartY=-7.80327 StartZ=0 EndX=2.58839 EndY=-7.69871 EndZ=0
    g43: LineSegment StartX=2.6542 StartY=-7.03945 StartZ=0 EndX=2.86963 EndY=-6.81749 EndZ=0
    g44: LineSegment StartX=2.86963 StartY=-6.81749 StartZ=0 EndX=3.0916 EndY=-6.92847 EndZ=0
    g45: LineSegment StartX=3.0916 StartY=-6.92847 StartZ=0 EndX=3.79666 EndY=-7.57478 EndZ=0
    g46: LineSegment StartX=3.79666 StartY=-7.57478 StartZ=0 EndX=3.93376 EndY=-7.50297 EndZ=0
    g47: LineSegment StartX=3.93376 StartY=-7.50297 StartZ=0 EndX=4.46256 EndY=-7.97301 EndZ=0
    g48: LineSegment StartX=4.46256 StartY=-7.97301 StartZ=0 EndX=4.68452 EndY=-7.92079 EndZ=0
    g49: LineSegment StartX=4.68452 StartY=-7.92079 StartZ=0 EndX=5.1154 EndY=-8.34513 EndZ=0
    g50: LineSegment StartX=5.1154 StartY=-8.34513 StartZ=0 EndX=5.32431 EndY=-8.28637 EndZ=0
    g51: LineSegment StartX=5.32431 StartY=-8.28637 StartZ=0 EndX=6.23668 EndY=-8.79564 EndZ=0
    g52: LineSegment StartX=6.23668 StartY=-8.79564 StartZ=0 EndX=6.50362 EndY=-8.76631 EndZ=0
    g53: LineSegment StartX=6.50362 StartY=-8.76631 StartZ=0 EndX=7.14802 EndY=-9.05537 EndZ=0
    g54: LineSegment StartX=7.14802 StartY=-9.05537 StartZ=0 EndX=8.04883 EndY=-9.18613 EndZ=0
    g55: LineSegment StartX=8.04883 StartY=-9.18613 StartZ=0 EndX=8.36847 EndY=-7.93662 EndZ=0
    g56: LineSegment StartX=8.36847 StartY=-7.93662 StartZ=0 EndX=8.49923 EndY=-7.79133 EndZ=0
    g57: LineSegment StartX=8.49923 StartY=-7.79133 StartZ=0 EndX=8.43477 EndY=-6.72206 EndZ=0
    g58: LineSegment StartX=8.43477 StartY=-6.72206 StartZ=0 EndX=8.58621 EndY=-6.47988 EndZ=0
    g59: LineSegment StartX=8.58621 StartY=-6.47988 StartZ=0 EndX=8.32296 EndY=-5.53178 EndZ=0
    g60: LineSegment StartX=8.32296 StartY=-5.53178 StartZ=0 EndX=8.43984 EndY=-5.19091 EndZ=0
    g61: LineSegment StartX=8.43984 StartY=-5.19091 StartZ=0 EndX=8.07426 EndY=-4.39307 EndZ=0
    g62: LineSegment StartX=8.07426 StartY=-4.39307 StartZ=0 EndX=8.04236 EndY=-4.17777 EndZ=0
    g63: LineSegment StartX=8.04236 StartY=-4.17777 StartZ=0 EndX=8.0902 EndY=-3.99438 EndZ=0
    g64: LineSegment StartX=8.4103 StartY=-4.11103 StartZ=0 EndX=8.72013 EndY=-4.0502 EndZ=0
    g65: LineSegment StartX=8.72013 StartY=-4.0502 StartZ=0 EndX=9.31817 EndY=-4.0502 EndZ=0
    g66: LineSegment StartX=9.31817 StartY=-4.0502 StartZ=0 EndX=9.82964 EndY=-4.15887 EndZ=0
    g67: LineSegment StartX=10.1326 StartY=-3.9675 StartZ=0 EndX=10.5175 EndY=-3.9623 EndZ=0
    g68: LineSegment StartX=10.5175 StartY=-3.9623 StartZ=0 EndX=10.8831 EndY=-3.97536 EndZ=0
    g69: LineSegment StartX=10.8831 StartY=-3.97536 StartZ=0 EndX=11.2245 EndY=-4.09431 EndZ=0
    g70: LineSegment StartX=11.2245 StartY=-4.09431 StartZ=0 EndX=11.6861 EndY=-3.91007 EndZ=0
    g71: LineSegment StartX=11.6861 StartY=-3.91007 StartZ=0 EndX=12.1039 EndY=-3.88396 EndZ=0
    g72: LineSegment StartX=12.1039 StartY=-3.88396 StartZ=0 EndX=12.6 EndY=-3.9623 EndZ=0
    g73: LineSegment StartX=12.6 StartY=-3.9623 StartZ=0 EndX=13.5793 EndY=-3.87743 EndZ=0
    g74: LineSegment StartX=13.5793 StartY=-3.87743 StartZ=0 EndX=14.3888 EndY=-3.74687 EndZ=0
    g75: LineSegment StartX=14.3888 StartY=-3.74687 StartZ=0 EndX=14.7544 EndY=-3.68158 EndZ=0
    g76: LineSegment StartX=14.7544 StartY=-3.68158 StartZ=0 EndX=15.2767 EndY=-3.75339 EndZ=0
    g77: LineSegment StartX=15.2767 StartY=-3.75339 StartZ=0 EndX=15.0432 EndY=-3.24137 EndZ=0
    g78: LineSegment StartX=15.0432 StartY=-3.24137 StartZ=0 EndX=14.5209 EndY=-2.51672 EndZ=0
    g79: LineSegment StartX=14.5209 StartY=-2.51672 StartZ=0 EndX=14.0378 EndY=-1.99445 EndZ=0
    g80: LineSegment StartX=14.0378 StartY=-1.99445 StartZ=0 EndX=13.2802 EndY=-1.54625 EndZ=0
    g81: LineSegment StartX=13.2802 StartY=-1.54625 StartZ=0 EndX=13.0438 EndY=-1.23117 EndZ=0
    g82: LineSegment StartX=13.0438 StartY=-1.23117 StartZ=0 EndX=12.1074 EndY=-0.797939 EndZ=0
    g83: LineSegment StartX=12.1074 StartY=-0.797939 StartZ=0 EndX=11.3804 EndY=-0.250878 EndZ=0
    g84: LineSegment StartX=11.3804 StartY=-0.250878 StartZ=0 EndX=10.4396 EndY=0.304889 EndZ=0
    g85: LineSegment StartX=10.4396 StartY=0.304889 StartZ=0 EndX=9.59526 EndY=0.727998 EndZ=0
    g86: LineSegment StartX=9.59526 StartY=0.727998 StartZ=0 EndX=8.53624 EndY=0.97306 EndZ=0
    g87: LineSegment StartX=8.53624 StartY=0.97306 StartZ=0 EndX=7.199 EndY=0.97306 EndZ=0
    g88: LineSegment StartX=7.199 StartY=0.97306 StartZ=0 EndX=5.77932 EndY=0.795578 EndZ=0
    g89: LineSegment StartX=5.77932 StartY=0.795578 StartZ=0 EndX=5.60186 EndY=0.795578 EndZ=0
    g90: LineSegment StartX=5.60186 StartY=0.795578 StartZ=0 EndX=5.83178 EndY=0.981815 EndZ=0
    g91: LineSegment StartX=5.83178 StartY=0.981815 StartZ=0 EndX=6.25403 EndY=1.1582 EndZ=0
    g92: LineSegment StartX=6.30214 StartY=1.38269 StartZ=0 EndX=7.17987 EndY=1.70686 EndZ=0
    g93: LineSegment StartX=7.17987 StartY=1.70686 StartZ=0 EndX=7.44682 EndY=1.79438 EndZ=0
    g94: LineSegment StartX=7.44682 StartY=1.79438 StartZ=0 EndX=7.49058 EndY=2.12696 EndZ=0
    g95: LineSegment StartX=7.49058 StartY=2.12696 StartZ=0 EndX=8.30058 EndY=2.66839 EndZ=0
    g96: LineSegment StartX=8.30058 StartY=2.66839 StartZ=0 EndX=8.68575 EndY=2.81854 EndZ=0
    g97: LineSegment StartX=8.68575 StartY=2.81854 StartZ=0 EndX=8.68575 EndY=3.12537 EndZ=0
    g98: LineSegment StartX=8.68575 StartY=3.12537 StartZ=0 EndX=8.89508 EndY=3.18684 EndZ=0
    g99: LineSegment StartX=8.89508 StartY=3.18684 StartZ=0 EndX=9.63492 EndY=4.06602 EndZ=0
    g100: LineSegment StartX=9.63492 StartY=4.06602 StartZ=0 EndX=9.62638 EndY=4.32743 EndZ=0
    g101: LineSegment StartX=9.62638 StartY=4.32743 StartZ=0 EndX=10.2068 EndY=5.18314 EndZ=0
    g102: LineSegment StartX=10.2068 StartY=5.18314 StartZ=0 EndX=9.25518 EndY=5.64445 EndZ=0
    g103: LineSegment StartX=9.1102 StartY=5.87597 StartZ=0 EndX=8.32132 EndY=5.97336 EndZ=0
    g104: LineSegment StartX=8.32132 StartY=5.97336 StartZ=0 EndX=8.15466 EndY=6.06625 EndZ=0
    g105: LineSegment StartX=7.63471 StartY=6.13088 StartZ=0 EndX=7.56391 EndY=6.33267 EndZ=0
    g106: LineSegment StartX=7.56391 StartY=6.33267 StartZ=0 EndX=6.74832 EndY=6.35496 EndZ=0
    g107: LineSegment StartX=6.74832 StartY=6.35496 StartZ=0 EndX=6.46819 EndY=6.29526 EndZ=0
    g108: LineSegment StartX=6.46819 StartY=6.29526 StartZ=0 EndX=6.27042 EndY=6.61061 EndZ=0
    g109: LineSegment StartX=6.27042 StartY=6.61061 StartZ=0 EndX=5.40453 EndY=6.33267 EndZ=0
    g110: LineSegment StartX=5.40453 StartY=6.33267 StartZ=0 EndX=5.27091 EndY=6.47164 EndZ=0
    g111: LineSegment StartX=5.27091 StartY=6.47164 StartZ=0 EndX=4.56942 EndY=6.24725 EndZ=0
    g112: LineSegment StartX=4.56942 StartY=6.24725 StartZ=0 EndX=4.44161 EndY=6.40652 EndZ=0
    g113: LineSegment StartX=4.44161 StartY=6.40652 StartZ=0 EndX=3.4195 EndY=5.94588 EndZ=0
    g114: LineSegment StartX=3.4195 StartY=5.94588 StartZ=0 EndX=3.29192 EndY=6.1532 EndZ=0
    g115: LineSegment StartX=3.29192 StartY=6.1532 StartZ=0 EndX=2.15964 EndY=5.49137 EndZ=0
    g116: LineSegment StartX=2.15964 StartY=5.49137 StartZ=0 EndX=2.00016 EndY=5.69869 EndZ=0
    g117: LineSegment StartX=2.00016 StartY=5.69869 StartZ=0 EndX=1.6185 EndY=5.34828 EndZ=0
    g118: LineSegment StartX=1.6185 StartY=5.34828 StartZ=0 EndX=1.45984 EndY=5.94974 EndZ=0
    g119: LineSegment StartX=1.38165 StartY=6.28651 StartZ=0 EndX=1.14534 EndY=6.29963 EndZ=0
    g120: LineSegment StartX=0.348522 StartY=7.29544 StartZ=0 EndX=0.126706 EndY=7.68126 EndZ=0
    g121: LineSegment StartX=0.126706 StartY=7.68126 StartZ=0 EndX=-0.415308 EndY=8.18163 EndZ=0
    g122: LineSegment StartX=-0.415308 StartY=8.18163 StartZ=0 EndX=-0.872658 EndY=8.6237 EndZ=0
    g123: LineSegment StartX=-0.872658 StartY=8.6237 StartZ=0 EndX=-1.12074 EndY=8.64329 EndZ=0
    g124: LineSegment StartX=-1.12074 StartY=8.64329 StartZ=0 EndX=-1.79316 EndY=9.11986 EndZ=0
    g125: LineSegment StartX=-1.79316 StartY=9.11986 StartZ=0 EndX=-2.31488 EndY=9.12122 EndZ=0
    g126: LineSegment StartX=-2.31488 StartY=9.12122 StartZ=0 EndX=-2.71321 EndY=9.13846 EndZ=0
    g127: LineSegment StartX=-2.71321 StartY=9.13846 StartZ=0 EndX=-2.88425 EndY=9.34157 EndZ=0
    g128: LineSegment StartX=-2.88425 StartY=9.34157 StartZ=0 EndX=-3.16779 EndY=9.26454 EndZ=0
    g129: LineSegment StartX=-3.70739 StartY=9.82796 StartZ=0 EndX=-4.04915 EndY=9.7003 EndZ=0
    g130: LineSegment StartX=-4.04915 StartY=9.7003 StartZ=0 EndX=-4.42988 EndY=10.011 EndZ=0
    g131: LineSegment StartX=-5.98947 StartY=10.3656 StartZ=0 EndX=-7.32605 EndY=10.4108 EndZ=0
    g132: LineSegment StartX=-7.25254 StartY=9.13254 StartZ=0 EndX=-7.36878 EndY=8.7693 EndZ=0
    g133: LineSegment StartX=-7.36878 StartY=8.7693 StartZ=0 EndX=-7.2614 EndY=7.83762 EndZ=0
    g134: LineSegment StartX=-7.2614 StartY=7.83762 StartZ=0 EndX=-7.41112 EndY=7.6042 EndZ=0
    g135: LineSegment StartX=-7.41112 StartY=7.6042 StartZ=0 EndX=-7.09216 EndY=6.74302 EndZ=0
    g136: LineSegment StartX=-7.09216 StartY=6.74302 StartZ=0 EndX=-7.10014 EndY=6.55962 EndZ=0
    g137: LineSegment StartX=-7.10014 StartY=6.55962 StartZ=0 EndX=-7.29151 EndY=6.3842 EndZ=0
    g138: LineSegment StartX=-7.29151 StartY=6.3842 StartZ=0 EndX=-6.74132 EndY=5.29976 EndZ=0
    g139: LineSegment StartX=-6.74132 StartY=5.29976 StartZ=0 EndX=-6.87495 EndY=5.02732 EndZ=0
    g140: LineSegment StartX=-6.87495 StartY=5.02732 StartZ=0 EndX=-6.31586 EndY=4.42065 EndZ=0
    g141: LineSegment StartX=-6.31586 StartY=4.42065 StartZ=0 EndX=-6.30396 EndY=4.19463 EndZ=0
    g142: LineSegment StartX=-6.30396 StartY=4.19463 StartZ=0 EndX=-6.05415 EndY=4.0043 EndZ=0
    g143: LineSegment StartX=-6.05415 StartY=4.0043 StartZ=0 EndX=-6.18501 EndY=3.95672 EndZ=0
    g144: LineSegment StartX=-6.18501 StartY=3.95672 StartZ=0 EndX=-5.54265 EndY=3.07645 EndZ=0
    g145: LineSegment StartX=-5.54265 StartY=3.07645 StartZ=0 EndX=-5.57833 EndY=2.90991 EndZ=0
    g146: LineSegment StartX=-5.57833 StartY=2.90991 StartZ=0 EndX=-5.1263 EndY=2.41029 EndZ=0
    g147: LineSegment StartX=-5.1263 StartY=2.41029 StartZ=0 EndX=-5.18578 EndY=2.26755 EndZ=0
    g148: LineSegment StartX=-5.18578 StartY=2.26755 StartZ=0 EndX=-4.73375 EndY=1.89878 EndZ=0
    g149: LineSegment StartX=-4.73375 StartY=1.89878 StartZ=0 EndX=-4.42446 EndY=1.5895 EndZ=0
    g150: LineSegment StartX=-4.42446 StartY=1.5895 StartZ=0 EndX=-5.31663 EndY=1.29211 EndZ=0
    g151: LineSegment StartX=-5.31663 StartY=1.29211 StartZ=0 EndX=-5.84004 EndY=1.08988 EndZ=0
    g152: LineSegment StartX=-5.84004 StartY=1.08988 StartZ=0 EndX=-6.04226 EndY=0.792495 EndZ=0
    g153: LineSegment StartX=-6.04226 StartY=0.792495 StartZ=0 EndX=-6.94632 EndY=0.994719 EndZ=0
    g154: LineSegment StartX=-6.94632 StartY=0.994719 StartZ=0 EndX=-7.19613 EndY=0.887659 EndZ=0
    g155: LineSegment StartX=-7.19613 StartY=0.887659 StartZ=0 EndX=-7.8147 EndY=1.0423 EndZ=0
    g156: LineSegment StartX=-7.8147 StartY=1.0423 StartZ=0 EndX=-8.02502 EndY=0.969153 EndZ=0
    g157: LineSegment StartX=-8.02502 StartY=0.969153 StartZ=0 EndX=-8.60267 EndY=1.03042 EndZ=0
    g158: LineSegment StartX=-8.60267 StartY=1.03042 StartZ=0 EndX=-8.8346 EndY=0.872878 EndZ=0
    g159: LineSegment StartX=-8.8346 StartY=0.872878 StartZ=0 EndX=-9.33349 EndY=0.929767 EndZ=0
    g160: LineSegment StartX=-9.33349 StartY=0.929767 StartZ=0 EndX=-9.66169 EndY=0.649695 EndZ=0
    g161: LineSegment StartX=-9.66169 StartY=0.649695 StartZ=0 EndX=-10.3249 EndY=0.649695 EndZ=0
    g162: LineSegment StartX=-10.3249 StartY=0.649695 StartZ=0 EndX=-11.0107 EndY=0.32425 EndZ=0
    g163: LineSegment StartX=-11.0107 StartY=0.32425 StartZ=0 EndX=-11.7283 EndY=0.053139 EndZ=0
    g164: LineSegment StartX=-11.7283 StartY=0.053139 StartZ=0 EndX=-12.2971 EndY=-0.13161 EndZ=0
    g165: LineSegment StartX=-12.2971 StartY=-0.13161 StartZ=0 EndX=-12.4212 EndY=-0.347049 EndZ=0
    g166: LineSegment StartX=-12.4212 StartY=-0.347049 StartZ=0 EndX=-13.296 EndY=-0.817096 EndZ=0
    g167: LineSegment StartX=-13.296 StartY=-0.817096 StartZ=0 EndX=-13.9227 EndY=-1.24144 EndZ=0
    g168: LineSegment StartX=-13.9227 StartY=-1.24144 StartZ=0 EndX=-14.1708 EndY=-1.59398 EndZ=0
    g169: LineSegment StartX=-14.1708 StartY=-1.59398 StartZ=0 EndX=-14.5386 EndY=-2.09216 EndZ=0
    g170: LineSegment StartX=-14.5386 StartY=-2.09216 StartZ=0 EndX=-14.7831 EndY=-2.4577 EndZ=0
    g171: LineSegment StartX=-14.7831 StartY=-2.4577 StartZ=0 EndX=-15.0667 EndY=-2.9879 EndZ=0
    g172: LineSegment StartX=7.82861 StartY=6.04487 StartZ=0 EndX=7.63471 EndY=6.13088 EndZ=0
    g173: LineSegment StartX=-14.4175 StartY=-3.20194 StartZ=0 EndX=-14.1386 EndY=-3.3581 EndZ=0
    g174: LineSegment StartX=-13.8673 StartY=-3.55064 StartZ=0 EndX=-13.4107 EndY=-3.57136 EndZ=0
    g175: LineSegment StartX=-13.1321 StartY=-3.61699 StartZ=0 EndX=-12.817 EndY=-3.62343 EndZ=0
    g176: LineSegment StartX=-12.817 StartY=-3.62343 StartZ=0 EndX=-12.4662 EndY=-3.85302 EndZ=0
    g177: LineSegment StartX=-13.4107 StartY=-3.57136 StartZ=0 EndX=-13.1321 EndY=-3.61699 EndZ=0
    g178: LineSegment StartX=-12.4662 StartY=-3.85302 StartZ=0 EndX=-11.8704 EndY=-3.85302 EndZ=0
    g179: LineSegment StartX=-11.8704 StartY=-3.85302 StartZ=0 EndX=-11.5204 EndY=-4.00836 EndZ=0
    g180: LineSegment StartX=-11.5204 StartY=-4.00836 StartZ=0 EndX=-11.1389 EndY=-4.05555 EndZ=0
    g181: LineSegment StartX=-11.1389 StartY=-4.05555 StartZ=0 EndX=-10.8098 EndY=-4.00788 EndZ=0
    g182: LineSegment StartX=-9.89036 StartY=-4.3898 StartZ=0 EndX=-9.99555 EndY=-4.87697 EndZ=0
    g183: LineSegment StartX=-9.99555 StartY=-4.87697 StartZ=0 EndX=-10.0894 EndY=-5.36391 EndZ=0
    g184: LineSegment StartX=-10.0894 StartY=-5.36391 StartZ=0 EndX=-10.107 EndY=-5.50471 EndZ=0
    g185: LineSegment StartX=-10.107 StartY=-5.50471 StartZ=0 EndX=-9.77848 EndY=-5.63965 EndZ=0
    g186: LineSegment StartX=-9.77848 StartY=-5.63965 StartZ=0 EndX=-9.51656 EndY=-5.73022 EndZ=0
    g187: LineSegment StartX=-4.19735 StartY=-5.16248 StartZ=0 EndX=-3.75191 EndY=-4.97251 EndZ=0
    g188: LineSegment StartX=-2.38042 StartY=-4.51801 StartZ=0 EndX=-2.15112 EndY=-4.35765 EndZ=0
    g189: LineSegment StartX=-3.4685 StartY=-8.65617 StartZ=0 EndX=-3.27268 EndY=-8.56671 EndZ=0
    g190: LineSegment StartX=-3.16823 StartY=-8.76909 StartZ=0 EndX=-3.07088 EndY=-9.32083 EndZ=0
    g191: LineSegment StartX=2.58839 StartY=-7.69871 StartZ=0 EndX=2.6542 EndY=-7.03945 EndZ=0
    g192: LineSegment StartX=8.0902 StartY=-3.99438 StartZ=0 EndX=8.4103 EndY=-4.11103 EndZ=0
    g193: LineSegment StartX=9.82964 StartY=-4.15887 StartZ=0 EndX=10.1326 EndY=-3.9675 EndZ=0
    g194: LineSegment StartX=6.30214 StartY=1.38269 StartZ=0 EndX=6.25403 EndY=1.1582 EndZ=0
    g195: LineSegment StartX=1.38165 StartY=6.28651 StartZ=0 EndX=1.45984 EndY=5.94974 EndZ=0
    g196: LineSegment StartX=0.348522 StartY=7.29544 StartZ=0 EndX=0.824344 EndY=6.91479 EndZ=0
    g197: LineSegment StartX=0.824344 StartY=6.91479 StartZ=0 EndX=1.14534 EndY=6.29963 EndZ=0
    g198: LineSegment StartX=-3.70739 StartY=9.82796 StartZ=0 EndX=-3.16779 EndY=9.26454 EndZ=0
    g199: LineSegment StartX=-5.98947 StartY=10.3656 StartZ=0 EndX=-5.43038 EndY=10.4489 EndZ=0
    g200: LineSegment StartX=-5.43038 StartY=10.4489 StartZ=0 EndX=-4.9791 EndY=10.1425 EndZ=0
    g201: LineSegment StartX=-4.42988 StartY=10.011 StartZ=0 EndX=-4.9791 EndY=10.1425 EndZ=0
    g202: LineSegment StartX=-7.25254 StartY=9.13254 StartZ=0 EndX=-7.32605 EndY=10.4108 EndZ=0
    g203: LineSegment StartX=7.82861 StartY=6.04487 StartZ=0 EndX=8.15466 EndY=6.06625 EndZ=0
    g204: LineSegment StartX=9.1102 StartY=5.87597 StartZ=0 EndX=9.25518 EndY=5.64445 EndZ=0
  constraints (114):
    c: Coincident(g4,g3)
    c: Coincident(g6,g5)
    c: Coincident(g8,g7)
    c: Coincident(g9,g8)
    c: Coincident(g10,g9)
    c: Coincident(g11,g10)
    c: Coincident(g13,g12)
    c: Coincident(g16,g15)
    c: Coincident(g22,g21)
    c: Coincident(g25,g24)
    c: Coincident(g26,g25)
    c: Coincident(g28,g27)
    c: Coincident(g33,g32)
    c: Coincident(g37,g36)
    c: Coincident(g38,g37)
    c: Coincident(g40,g39)
    c: Coincident(g44,g43)
    c: Coincident(g51,g50)
    c: Coincident(g52,g51)
    c: Coincident(g57,g56)
    c: Coincident(g58,g57)
    c: Coincident(g59,g58)
    c: Coincident(g61,g60)
    c: Coincident(g63,g62)
    c: Coincident(g66,g65)
    c: Coincident(g70,g69)
    c: Coincident(g72,g71)
    c: Coincident(g73,g72)
    c: Coincident(g74,g73)
    c: Coincident(g77,g76)
    c: Coincident(g80,g79)
    c: Coincident(g81,g80)
    c: Coincident(g83,g82)
    c: Coincident(g85,g84)
    c: Coincident(g86,g85)
    c: Coincident(g87,g86)
    c: Coincident(g89,g88)
    c: Coincident(g90,g89)
    c: Coincident(g91,g90)
    c: Coincident(g93,g92)
    c: Coincident(g95,g94)
    c: Coincident(g97,g96)
    c: Coincident(g98,g97)
    c: Coincident(g99,g98)
    c: Coincident(g100,g99)
    c: Coincident(g104,g103)
    c: Coincident(g106,g105)
    c: Coincident(g107,g106)
    c: Coincident(g111,g110)
    c: Coincident(g113,g112)
    c: Coincident(g118,g117)
    c: Coincident(g122,g121)
    c: Coincident(g126,g125)
    c: Coincident(g130,g129)
    c: Coincident(g133,g132)
    c: Coincident(g134,g133)
    c: Coincident(g135,g134)
    c: Coincident(g139,g138)
    c: Coincident(g142,g141)
    c: Coincident(g156,g155)
    c: Coincident(g157,g156)
    c: Coincident(g159,g158)
    c: Coincident(g161,g160)
    c: Coincident(g164,g163)
    c: Coincident(g165,g164)
    c: Coincident(g168,g167)
    c: Coincident(g169,g168)
    c: Coincident(g171,g170)
    c: Coincident(g171,g0)
    c: Coincident(g172,g105)
    c: DistanceX(g165) = -12.4212
    c: DistanceY(g165) = -0.347049
    c: Coincident(g173,g0)
    c: Coincident(g173,g1)
    c: Coincident(g174,g1)
    c: Coincident(g177,g174)
    c: Coincident(g177,g175)
    c: Coincident(g178,g176)
    c: Coincident(g181,g2)
    c: Coincident(g182,g4)
    c: Coincident(g186,g185)
    c: Coincident(g186,g5)
    c: Coincident(g187,g16)
    c: Coincident(g187,g17)
    c: Coincident(g188,g21)
    c: Coincident(g188,g20)
    c: Coincident(g189,g28)
    c: Coincident(g189,g29)
    c: Coincident(g190,g29)
    c: Coincident(g190,g30)
    c: Coincident(g191,g42)
    c: Coincident(g191,g43)
    c: Coincident(g192,g63)
    c: Coincident(g192,g64)
    c: Coincident(g193,g66)
    c: Coincident(g193,g67)
    c: Coincident(g194,g92)
    c: Coincident(g194,g91)
    c: Coincident(g195,g119)
    c: Coincident(g195,g118)
    c: Coincident(g196,g120)
    c: Coincident(g197,g119)
    c: Coincident(g198,g129)
    c: Coincident(g198,g128)
    c: Coincident(g199,g131)
    c: Coincident(g200,g199)
    c: Coincident(g201,g130)
    c: Coincident(g201,g200)
    c: Coincident(g202,g132)
    c: Coincident(g202,g131)
    c: Coincident(g203,g172)
    c: Coincident(g203,g104)
    c: Coincident(g204,g103)
    c: Coincident(g204,g102)
FEATURE [PartDesign::Pad] Pad002
  Direction = (0,0,1)
  Length = 3
  Length2 = 10
  Profile = -> Sketch002
  ReferenceAxis = -> Sketch002 [N_Axis]
  Type = 0
FEATURE [PartDesign::Body] Body002  label="logo004"
  Group = -> [Sketch002,Pad002]
  Origin = -> Origin002
  Placement = pos=(39.35,-43,30) rot=(1,0,0;1.5708rad)
  Tip = -> Pad002
FEATURE [Part::MultiFuse] Fusion041  label="logo"
  Placement = pos=(-69,-26,58) rot=(1,0,0;3.14159rad)
  Shapes = -> [Body002,Box069]
FEATURE [Part::MultiFuse] Fusion006  label="back001"
  Shapes = -> [Cut007,Box021]
FEATURE [Part::MultiFuse] Fusion042
  Shapes = -> [Fusion006,Cut008]
FEATURE [Part::Cylinder] Cylinder011
  Angle = 90
  AttacherType = Attacher::AttachEngine3D
  FirstAngle = 0
  Height = 65.2
  Placement = pos=(-50,18,-45.4) rot=(0,0,1;1.5708rad)
  Radius = 2
  SecondAngle = 0
FEATURE [Part::Box] Box070  label="Cube010"
  AttacherType = Attacher::AttachEngine3D
  Height = 20
  Length = 1.7
  Placement = pos=(-50.3,0.2,-10) rot=(0,1,0;3.14159rad)
  Width = 17.8
FEATURE [Part::Box] Box071  label="Cube011"
  AttacherType = Attacher::AttachEngine3D
  Height = 10
  Length = 23
  Placement = pos=(50.3,-5,-54.4) rot=(0,0,1;1.5708rad)
  Width = 100.6
FEATURE [Part::MultiFuse] Fusion043
  Shapes = -> [Box070,Cylinder011,Fusion042]
FEATURE [Part::Cut] Cut009
  Base = -> Fusion043
  Tool = -> Box071
